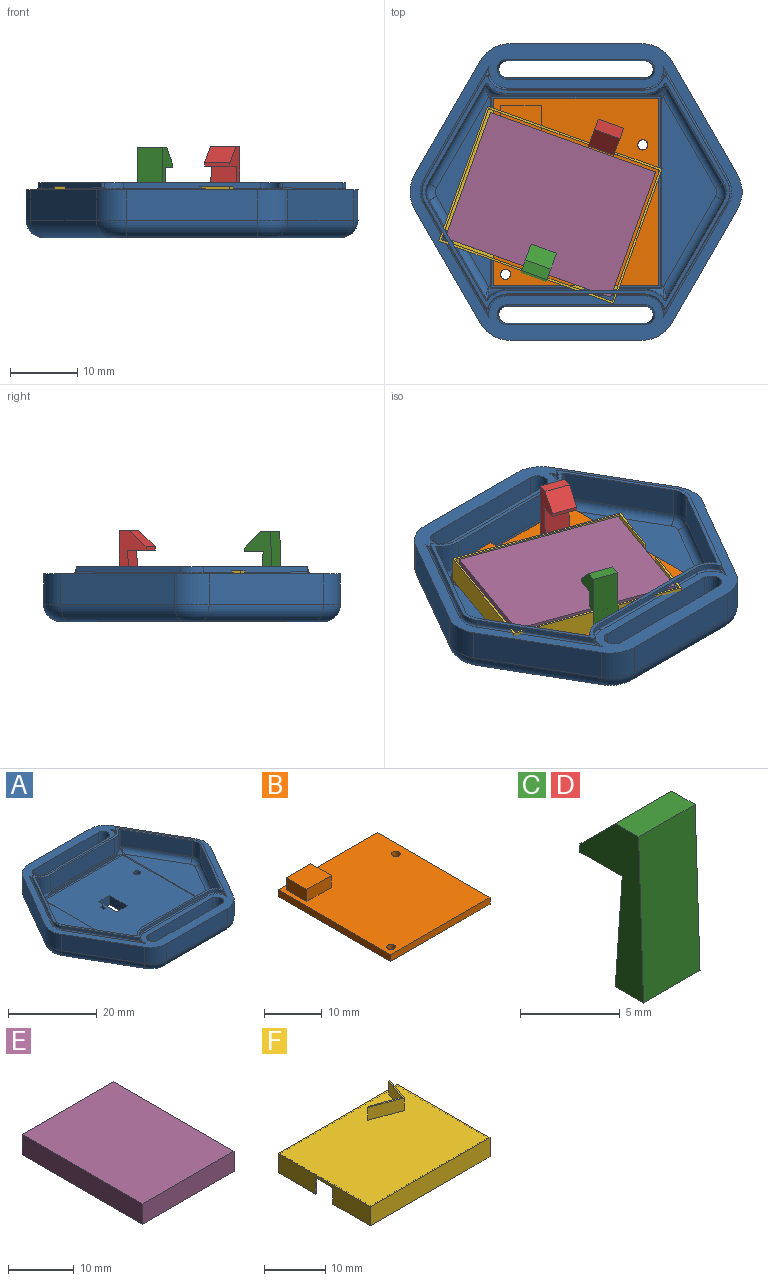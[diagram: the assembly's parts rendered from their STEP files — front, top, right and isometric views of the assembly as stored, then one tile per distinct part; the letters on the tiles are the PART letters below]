
ASSEMBLY  parts=6 mates=3
PART A: 135 faces, bbox 50.4x45.1x12.3 mm
  f0: bspline ~0.45x0.19mm, area 0mm2, adj f109,f110,f133,f134
  f1: bspline ~0.45x0.18mm, area 0mm2, adj f69,f104,f106,f131,f132
  f2: bspline ~0.45x0.18mm, area 0mm2, adj f63,f103,f105,f129,f130
  f3: bspline ~0.45x0.19mm, area 0mm2, adj f99,f100,f127,f128
  f4: plane 28x8.15mm, normal (0,0,1), area 120.5mm2, adj f83,f84,f85,f86,f88,f120
  f5: plane 49.23x43.99mm, normal (0,0,1), area 331.2mm2, adj f8,f9,f10,f12,f14,f16,f17,f18
  f6: torus R=2.54mm, axis (0,0,1), area 17.4mm2, adj f7,f19,f35,f36
  f7: cylinder r=2.54mm len=18.19mm, axis (0.5,-0.87,0), area 77.9mm2, adj f6,f8,f19,f28
  f8: plane 16.92x9.77mm, normal (-0.87,-0.5,0), area 88.7mm2, adj f5,f7,f9,f35
  f9: cylinder r=5.08mm len=4.54mm, axis (0,0,-1), area 24.2mm2, adj f5,f8,f10,f28
  f10: plane 19.53x4.54mm, normal (0,-1,0), area 88.7mm2, adj f5,f9,f12,f29
  f11: cylinder r=2.54mm len=18.19mm, axis (0.5,0.87,0), area 77.9mm2, adj f13,f14,f19,f30
  f12: cylinder r=5.08mm len=4.54mm, axis (0,0,-1), area 24.2mm2, adj f5,f10,f14,f30
  f13: torus R=2.54mm, axis (0,0,1), area 17.4mm2, adj f11,f15,f16,f19
  f14: plane 16.92x9.77mm, normal (0.87,-0.5,0), area 88.7mm2, adj f5,f11,f12,f16
  f15: cylinder r=2.54mm len=18.19mm, axis (-0.5,0.87,0), area 77.9mm2, adj f13,f17,f19,f21
  f16: cylinder r=5.08mm len=5.08mm, axis (0,0,-1), area 24.2mm2, adj f5,f13,f14,f17
  f17: plane 16.92x9.77mm, normal (0.87,0.5,0), area 88.7mm2, adj f5,f15,f16,f18
  f18: cylinder r=5.08mm len=4.54mm, axis (0,0,-1), area 24.2mm2, adj f5,f17,f21,f34
  f19: plane 44.15x38.27mm, normal (0,0,-1), area 1168.4mm2, adj f6,f7,f11,f13,f15,f20,f21,f23
  f20: plane 20.32x7.08mm, normal (0,1,0.03), area 144mm2, adj f5,f19,f24,f25
  f21: torus R=2.54mm, axis (0,0,1), area 17.3mm2, adj f15,f18,f19,f22,f25,f26
  f22: cylinder r=2.54mm len=19.53mm, axis (-1,0,0), area 77.9mm2, adj f21,f23,f26,f34
  f23: torus R=2.54mm, axis (0,0,1), area 17.3mm2, adj f19,f22,f24,f26,f36,f37
  f24: cone r=1.27mm half-angle=2deg, axis (0,0,1), area 31mm2, adj f5,f19,f20,f23,f26
  f25: cone r=1.27mm half-angle=2deg, axis (0,0,1), area 31mm2, adj f5,f19,f20,f21,f26
  f26: plane 20.34x7.1mm, normal (0,-1,0.03), area 144mm2, adj f5,f21,f22,f23,f24,f25
  f27: plane 20.32x7.08mm, normal (0,-1,0.03), area 144mm2, adj f5,f19,f31,f32
  f28: torus R=2.54mm, axis (0,0,1), area 17.3mm2, adj f7,f9,f19,f29,f32,f33
  f29: cylinder r=2.54mm len=19.53mm, axis (1,0,0), area 77.9mm2, adj f10,f28,f30,f33
  f30: torus R=2.54mm, axis (0,0,1), area 17.3mm2, adj f11,f12,f19,f29,f31,f33
  f31: cone r=1.27mm half-angle=2deg, axis (0,0,1), area 31mm2, adj f5,f19,f27,f30,f33
  f32: cone r=1.27mm half-angle=2deg, axis (0,0,1), area 31mm2, adj f5,f19,f27,f28,f33
  f33: plane 20.34x7.1mm, normal (0,1,0.03), area 144mm2, adj f5,f28,f29,f30,f31,f32
  f34: plane 19.53x4.54mm, normal (0,1,0), area 88.7mm2, adj f5,f18,f22,f37
  f35: cylinder r=5.08mm len=5.08mm, axis (0,0,-1), area 24.2mm2, adj f5,f6,f8,f38
  f36: cylinder r=2.54mm len=18.19mm, axis (-0.5,-0.87,0), area 77.9mm2, adj f6,f19,f23,f38
  f37: cylinder r=5.08mm len=4.54mm, axis (0,0,-1), area 24.2mm2, adj f5,f23,f34,f38
  f38: plane 16.92x9.77mm, normal (-0.87,0.5,0), area 88.7mm2, adj f5,f35,f36,f37
  f39: cone r=3.81mm half-angle=2deg, axis (0,0,-1), area 14.2mm2, adj f40,f71,f89,f113
  f40: plane 20.32x4.32mm, normal (0,-1,0.03), area 87.9mm2, adj f39,f41,f71,f87
  f41: cone r=3.81mm half-angle=2deg, axis (0,0,-1), area 14.2mm2, adj f40,f71,f85,f111
  f42: plane 14.68x8.45mm, normal (-0.87,-0.5,0.03), area 72.5mm2, adj f43,f71,f83,f111
  f43: cone r=2.54mm half-angle=2deg, axis (0,0,1), area 12.1mm2, adj f42,f44,f71,f84
  f44: plane 14.68x8.45mm, normal (-0.87,0.5,0.03), area 72.5mm2, adj f43,f71,f86,f115
  f45: cone r=3.81mm half-angle=2deg, axis (0,0,-1), area 14.2mm2, adj f46,f71,f88,f115
  f46: plane 20.32x4.32mm, normal (0,1,0.03), area 87.9mm2, adj f45,f47,f71,f90
  f47: cone r=3.81mm half-angle=2deg, axis (0,0,-1), area 14.2mm2, adj f46,f71,f92,f117
  f48: plane 14.68x8.45mm, normal (0.87,0.5,0.03), area 72.5mm2, adj f49,f71,f94,f117
  f49: cone r=2.54mm half-angle=2deg, axis (0,0,1), area 12.1mm2, adj f48,f50,f71,f93
  f50: plane 14.68x8.45mm, normal (0.87,-0.5,0.03), area 72.5mm2, adj f49,f71,f91,f113
  f51: plane 28x8.15mm, normal (0,0,1), area 120.5mm2, adj f89,f91,f92,f93,f94,f125
  f52: plane 24.98x0.99mm, normal (0,1,0), area 15.6mm2, adj f88,f90,f92,f121
  f53: plane 24.98x0.99mm, normal (0,-1,0), area 15.6mm2, adj f85,f87,f89,f124
  f54: plane 28.17x24.99mm, normal (0,0,1), area 680.2mm2, adj f55,f56,f57,f58,f72,f73,f74,f75
  f55: plane 3.4x2.44mm, normal (0,-1,0.03), area 8.1mm2, adj f19,f54,f56,f58
  f56: plane 5.72x2.44mm, normal (-1,0,0.03), area 13.7mm2, adj f19,f54,f55,f57
  f57: plane 3.4x2.44mm, normal (0,1,0.03), area 8.1mm2, adj f19,f54,f56,f58
  f58: plane 5.72x2.44mm, normal (1,0,0.03), area 13.7mm2, adj f19,f54,f55,f57
  f59: cone r=3.3mm half-angle=2deg, axis (0,0,-1), area 2.6mm2, adj f60,f70,f71,f108
  f60: plane 15.49x8.94mm, normal (0.87,0.5,0.03), area 13.3mm2, adj f59,f71,f110,f133
  f61: cone r=3.05mm half-angle=2deg, axis (0,0,1), area 2.7mm2, adj f62,f71,f109,f133
  f62: plane 20.32x0.76mm, normal (0,1,0.03), area 15.5mm2, adj f61,f63,f71,f107
  f63: cone r=3.05mm half-angle=2deg, axis (0,0,1), area 2.8mm2, adj f2,f62,f71,f105,f129
  f64: plane 15.49x8.94mm, normal (-0.87,0.5,0.03), area 13.6mm2, adj f65,f71,f103,f129
  f65: cone r=3.3mm half-angle=2deg, axis (0,0,-1), area 2.6mm2, adj f64,f66,f71,f101
  f66: plane 15.49x8.94mm, normal (-0.87,-0.5,0.03), area 13.3mm2, adj f65,f71,f99,f127
  f67: cone r=3.05mm half-angle=2deg, axis (0,0,1), area 2.7mm2, adj f68,f71,f100,f127
  f68: plane 20.32x0.76mm, normal (0,-1,0.03), area 15.5mm2, adj f67,f69,f71,f102
  f69: cone r=3.05mm half-angle=2deg, axis (0,0,1), area 2.8mm2, adj f1,f68,f71,f104,f131
  f70: plane 15.49x8.94mm, normal (0.87,-0.5,0.03), area 13.6mm2, adj f59,f71,f106,f131
  f71: plane 45.63x34.38mm, normal (0,0,1), area 70.7mm2, adj f39,f40,f41,f42,f43,f44,f45,f46
  f72: plane 1.2x1.14mm, normal (1,0,0.03), area 1.3mm2, adj f54,f73,f75,f97
  f73: plane 1.2x0.64mm, normal (0,-1,0.03), area 0.7mm2, adj f54,f72,f74,f98
  f74: plane 1.2x1.14mm, normal (-1,0,0.03), area 1.3mm2, adj f54,f73,f75,f96
  f75: plane 1.2x0.64mm, normal (0,1,0.03), area 0.7mm2, adj f54,f72,f74,f95
  f76: plane 0.66x0.15mm, normal (0,0,1), area 0.1mm2, adj f95,f96,f97,f98
  f77: cylinder r=1.25mm len=2.5mm, axis (0,0,-1), area 11mm2, adj f19,f78
  f78: plane 2.5x2.5mm, normal (0,0,-1), area 3.1mm2, adj f77,f81
  f79: cylinder r=1.25mm len=2.5mm, axis (0,0,-1), area 11mm2, adj f19,f80
  f80: plane 2.5x2.5mm, normal (0,0,-1), area 3.1mm2, adj f79,f82
  f81: cylinder r=0.75mm len=1.5mm, axis (0,0,-1), area 4.9mm2, adj f54,f78
  f82: cylinder r=0.75mm len=1.5mm, axis (0,0,-1), area 4.9mm2, adj f54,f80
  f83: cylinder r=1.28mm len=15.05mm, axis (-0.5,0.87,0), area 31.4mm2, adj f4,f42,f84,f112
  f84: torus R=1.31mm, axis (0,0,1), area 4.3mm2, adj f4,f43,f83,f86
  f85: torus R=5.04mm, axis (0,0,1), area 3.3mm2, adj f4,f41,f53,f87,f112,f122,f124
  f86: cylinder r=1.28mm len=15.05mm, axis (0.5,0.87,0), area 31.4mm2, adj f4,f44,f84,f116
  f87: cylinder r=1.28mm len=20.32mm, axis (-1,0,0), area 7.9mm2, adj f40,f53,f85,f89
  f88: torus R=5.04mm, axis (0,0,1), area 3.3mm2, adj f4,f45,f52,f90,f116,f119,f121
  f89: torus R=5.04mm, axis (0,0,1), area 3.3mm2, adj f39,f51,f53,f87,f114,f124,f126
  f90: cylinder r=1.28mm len=20.32mm, axis (1,0,0), area 7.9mm2, adj f46,f52,f88,f92
  f91: cylinder r=1.28mm len=15.05mm, axis (-0.5,-0.87,0), area 31.4mm2, adj f50,f51,f93,f114
  f92: torus R=5.04mm, axis (0,0,1), area 3.3mm2, adj f47,f51,f52,f90,f118,f121,f123
  f93: torus R=1.31mm, axis (0,0,1), area 4.3mm2, adj f49,f51,f91,f94
  f94: cylinder r=1.28mm len=15.05mm, axis (0.5,-0.87,0), area 31.4mm2, adj f48,f51,f93,f118
  f95: cylinder r=0.2mm len=0.55mm, axis (-1,0,0), area 0.1mm2, adj f75,f76,f96,f97
  f96: cylinder r=0.2mm len=1.06mm, axis (0,-1,0), area 0.3mm2, adj f74,f76,f95,f98
  f97: cylinder r=0.2mm len=1.06mm, axis (0,1,0), area 0.3mm2, adj f72,f76,f95,f98
  f98: cylinder r=0.2mm len=0.55mm, axis (1,0,0), area 0.1mm2, adj f73,f76,f96,f97
  f99: cylinder r=0.27mm len=16.91mm, axis (-0.5,0.87,0), area 7.5mm2, adj f3,f5,f66,f101,f128
  f100: torus R=2.79mm, axis (0,0,1), area 1.6mm2, adj f3,f5,f67,f102,f128
  f101: torus R=3.56mm, axis (0,0,1), area 1.4mm2, adj f5,f65,f99,f103
  f102: cylinder r=0.27mm len=20.32mm, axis (-1,0,0), area 8.3mm2, adj f5,f68,f100,f104
  f103: cylinder r=0.27mm len=16.91mm, axis (0.5,0.87,0), area 7.5mm2, adj f2,f5,f64,f101,f130
  f104: torus R=2.79mm, axis (0,0,1), area 1.6mm2, adj f1,f5,f69,f102,f132
  f105: torus R=2.79mm, axis (0,0,1), area 1.6mm2, adj f2,f5,f63,f107,f130
  f106: cylinder r=0.27mm len=16.91mm, axis (-0.5,-0.87,0), area 7.5mm2, adj f1,f5,f70,f108,f132
  f107: cylinder r=0.27mm len=20.32mm, axis (1,0,0), area 8.3mm2, adj f5,f62,f105,f109
  f108: torus R=3.56mm, axis (0,0,1), area 1.4mm2, adj f5,f59,f106,f110
  f109: torus R=2.79mm, axis (0,0,1), area 1.6mm2, adj f0,f5,f61,f107,f134
  f110: cylinder r=0.27mm len=16.91mm, axis (0.5,-0.87,0), area 7.5mm2, adj f0,f5,f60,f108,f134
  f111: bspline ~10.18x0.98mm, area 2.2mm2, adj f41,f42,f71,f112
  f112: bspline ~2.03x1.36mm, area 0.5mm2, adj f83,f85,f111
  f113: bspline ~10.18x0.98mm, area 2.2mm2, adj f39,f50,f71,f114
  f114: bspline ~2.03x1.36mm, area 0.5mm2, adj f89,f91,f113
  f115: bspline ~10.18x0.98mm, area 2.2mm2, adj f44,f45,f71,f116
  f116: bspline ~2.03x1.36mm, area 0.5mm2, adj f86,f88,f115
  f117: bspline ~10.18x0.98mm, area 2.2mm2, adj f47,f48,f71,f118
  f118: bspline ~2.03x1.36mm, area 0.5mm2, adj f92,f94,f117
  f119: bspline ~0.67x0.25mm, area 0.1mm2, adj f54,f88,f120,f121
  f120: cylinder r=0.27mm len=27.67mm, axis (0,-1,0), area 6.6mm2, adj f4,f54,f119,f122
  f121: cylinder r=0.27mm len=25.4mm, axis (1,0,0), area 10.5mm2, adj f52,f54,f88,f92,f119,f123
  f122: bspline ~0.76x0.26mm, area 0.1mm2, adj f54,f85,f120,f124
  f123: bspline ~0.76x0.26mm, area 0.1mm2, adj f54,f92,f121,f125
  f124: cylinder r=0.27mm len=25.4mm, axis (-1,0,0), area 10.5mm2, adj f53,f54,f85,f89,f122,f126
  f125: cylinder r=0.27mm len=27.67mm, axis (0,1,0), area 6.6mm2, adj f51,f54,f123,f126
  f126: bspline ~0.67x0.25mm, area 0.1mm2, adj f54,f89,f124,f125
  f127: bspline ~8.55x1.19mm, area 0.4mm2, adj f3,f66,f67,f71
  f128: bspline ~1.44x0.52mm, area 0.2mm2, adj f3,f99,f100
  f129: bspline ~8.55x1.19mm, area 0.4mm2, adj f2,f63,f64,f71
  f130: bspline ~1.44x0.52mm, area 0.2mm2, adj f2,f103,f105
  f131: bspline ~8.55x1.19mm, area 0.4mm2, adj f1,f69,f70,f71
  f132: bspline ~1.44x0.52mm, area 0.2mm2, adj f1,f104,f106
  f133: bspline ~8.55x1.19mm, area 0.4mm2, adj f0,f60,f61,f71
  f134: bspline ~1.44x0.52mm, area 0.2mm2, adj f0,f109,f110
PART B: 18 faces, bbox 24.4x27.7x5.6 mm
  f0: plane 27.69x24.38mm, normal (0,0,1), area 641.4mm2, adj f2,f3,f4,f5,f6,f7,f13,f14
  f1: plane 27.69x24.38mm, normal (0,0,-1), area 652mm2, adj f2,f3,f4,f5,f6,f7,f8,f9
  f2: plane 27.69x1.42mm, normal (1,0,0), area 39.3mm2, adj f0,f1,f3,f5
  f3: plane 24.38x1.42mm, normal (0,1,0), area 34.6mm2, adj f0,f1,f2,f4
  f4: plane 27.69x1.42mm, normal (-1,0,0), area 39.3mm2, adj f0,f1,f3,f5
  f5: plane 24.38x1.42mm, normal (0,-1,0), area 34.6mm2, adj f0,f1,f2,f4
  f6: cylinder r=0.76mm len=1.52mm, axis (0,0,-1), area 6.8mm2, adj f0,f1
  f7: cylinder r=0.76mm len=1.52mm, axis (0,0,-1), area 6.8mm2, adj f0,f1
  f8: plane 5.72x1.65mm, normal (1,0,0), area 9.4mm2, adj f1,f9,f11,f12
  f9: plane 3.4x1.65mm, normal (0,-1,0), area 5.6mm2, adj f1,f8,f10,f12
  f10: plane 5.72x1.65mm, normal (-1,0,0), area 9.4mm2, adj f1,f9,f11,f12
  f11: plane 3.4x1.65mm, normal (0,1,0), area 5.6mm2, adj f1,f8,f10,f12
  f12: plane 5.72x3.4mm, normal (0,0,-1), area 19.5mm2, adj f8,f9,f10,f11
  f13: plane 5x2.55mm, normal (-1,0,0), area 12.8mm2, adj f0,f14,f16,f17
  f14: plane 6x2.55mm, normal (0,-1,0), area 15.3mm2, adj f0,f13,f15,f17
  f15: plane 5x2.55mm, normal (1,0,0), area 12.8mm2, adj f0,f14,f16,f17
  f16: plane 6x2.55mm, normal (0,1,0), area 15.3mm2, adj f0,f13,f15,f17
  f17: plane 6x5mm, normal (0,0,1), area 30mm2, adj f13,f14,f15,f16
PART C: 9 faces, bbox 4x4.5x10 mm
  f0: plane 10x4.5mm, normal (-1,0,0), area 20.9mm2, adj f1,f3,f4,f5,f6,f7,f8
  f1: plane 10x4mm, normal (0,-1,0.03), area 40mm2, adj f0,f2,f4,f5
  f2: plane 10x4.5mm, normal (1,0,0), area 20.9mm2, adj f1,f3,f4,f5,f6,f7,f8
  f3: plane 7x4mm, normal (0,1,0.07), area 28.1mm2, adj f0,f2,f5,f6
  f4: plane 4x1.65mm, normal (0,0,1), area 6.6mm2, adj f0,f1,f2,f8
  f5: plane 4x2mm, normal (0,0,-1), area 8mm2, adj f0,f1,f2,f3
  f6: plane 4x2.99mm, normal (0,0,-1), area 12mm2, adj f0,f2,f3,f7
  f7: plane 4x0.5mm, normal (0,1,0), area 2mm2, adj f0,f2,f6,f8
  f8: plane 4x2.5mm, normal (0,0.71,0.71), area 14.1mm2, adj f0,f2,f4,f7
PART D: same geometry as C
PART E: 6 faces, bbox 19.8x26x3.8 mm
  f0: plane 26.02x3.8mm, normal (-1,0,0), area 98.9mm2, adj f1,f3,f4,f5
  f1: plane 19.75x3.8mm, normal (0,-1,0), area 75mm2, adj f0,f2,f4,f5
  f2: plane 26.02x3.8mm, normal (1,0,0), area 98.9mm2, adj f1,f3,f4,f5
  f3: plane 19.75x3.8mm, normal (0,1,0), area 75mm2, adj f0,f2,f4,f5
  f4: plane 26.02x19.75mm, normal (0,0,1), area 513.9mm2, adj f0,f1,f2,f3
  f5: plane 26.02x19.75mm, normal (0,0,-1), area 513.9mm2, adj f0,f1,f2,f3
PART F: 21 faces, bbox 27.5x21.3x6.4 mm
  f0: plane 27.52x21.25mm, normal (0,0,-1), area 27.7mm2, adj f1,f2,f3,f4,f5,f6,f7,f8
  f1: plane 20.65x3.7mm, normal (1,0,0), area 63.2mm2, adj f0,f4,f8,f9,f10,f11,f12
  f2: plane 21.25x3.8mm, normal (-1,0,0), area 67.5mm2, adj f0,f5,f7,f10,f11,f12,f19
  f3: plane 20.65x3.7mm, normal (-1,0,0), area 76.4mm2, adj f0,f4,f8,f9
  f4: plane 26.92x3.7mm, normal (0,1,0), area 99.6mm2, adj f0,f1,f3,f9
  f5: plane 27.52x3.8mm, normal (0,-1,0), area 104.6mm2, adj f0,f2,f6,f19
  f6: plane 21.25x3.8mm, normal (1,0,0), area 80.8mm2, adj f0,f5,f7,f19
  f7: plane 27.52x3.8mm, normal (0,1,0), area 104.6mm2, adj f0,f2,f6,f19
  f8: plane 26.92x3.7mm, normal (0,-1,0), area 99.6mm2, adj f0,f1,f3,f9
  f9: plane 26.92x20.65mm, normal (0,0,-1), area 555.9mm2, adj f1,f3,f4,f8
  f10: plane 3.3x0.3mm, normal (0,1,0), area 1mm2, adj f0,f1,f2,f11
  f11: plane 4x0.3mm, normal (0,0,-1), area 1.2mm2, adj f1,f2,f10,f12
  f12: plane 3.3x0.3mm, normal (0,-1,0), area 1mm2, adj f0,f1,f2,f11
  f13: plane 2.55x0.31mm, normal (-0.38,0.92,0), area 0.9mm2, adj f14,f18,f19,f20
  f14: plane 5.15x2.55mm, normal (0.94,-0.34,0), area 14mm2, adj f13,f15,f19,f20
  f15: plane 6.12x2.55mm, normal (-0.34,-0.94,0), area 16.6mm2, adj f14,f16,f19,f20
  f16: plane 2.55x0.32mm, normal (-0.43,0.9,0), area 0.9mm2, adj f15,f17,f19,f20
  f17: plane 5.65x2.55mm, normal (0.34,0.94,0), area 15.3mm2, adj f16,f18,f19,f20
  f18: plane 4.7x2.55mm, normal (-0.94,0.34,0), area 12.7mm2, adj f13,f17,f19,f20
  f19: plane 27.52x21.25mm, normal (0,0,1), area 581.9mm2, adj f2,f5,f6,f7,f13,f14,f15,f16
  f20: plane 7.97x5.15mm, normal (0,0,1), area 2.9mm2, adj f13,f14,f15,f16,f17,f18
PLACE A at identity fixed
PLACE B t=(0,0,-3.93)mm
PLACE C rot(axis=(0,0,-1),20deg) t=(4.51,10.03,3.39)mm
PLACE D rot(axis=(0,0.02,1),160.2deg) t=(19.76,31.44,3.44)mm
PLACE E rot(axis=(0.82,0.57,0),180deg) t=(-6.67,15.19,7.62)mm
PLACE F rot(axis=(-0.17,-0.99,0),180deg) t=(18.26,5.42,3.72)mm
MATE fastened B.f7 <-> A.f77  axis (0,0,-1) through (22.61,28.98,2.44)mm
MATE fastened E.f4 <-> F.f9  axis (0,0,-1) through (8.92,20.07,3.82)mm
MATE parallel C.f5 <-> B.f6  axis (0,0,-1) through (6.73,10.29,3.39)mm
